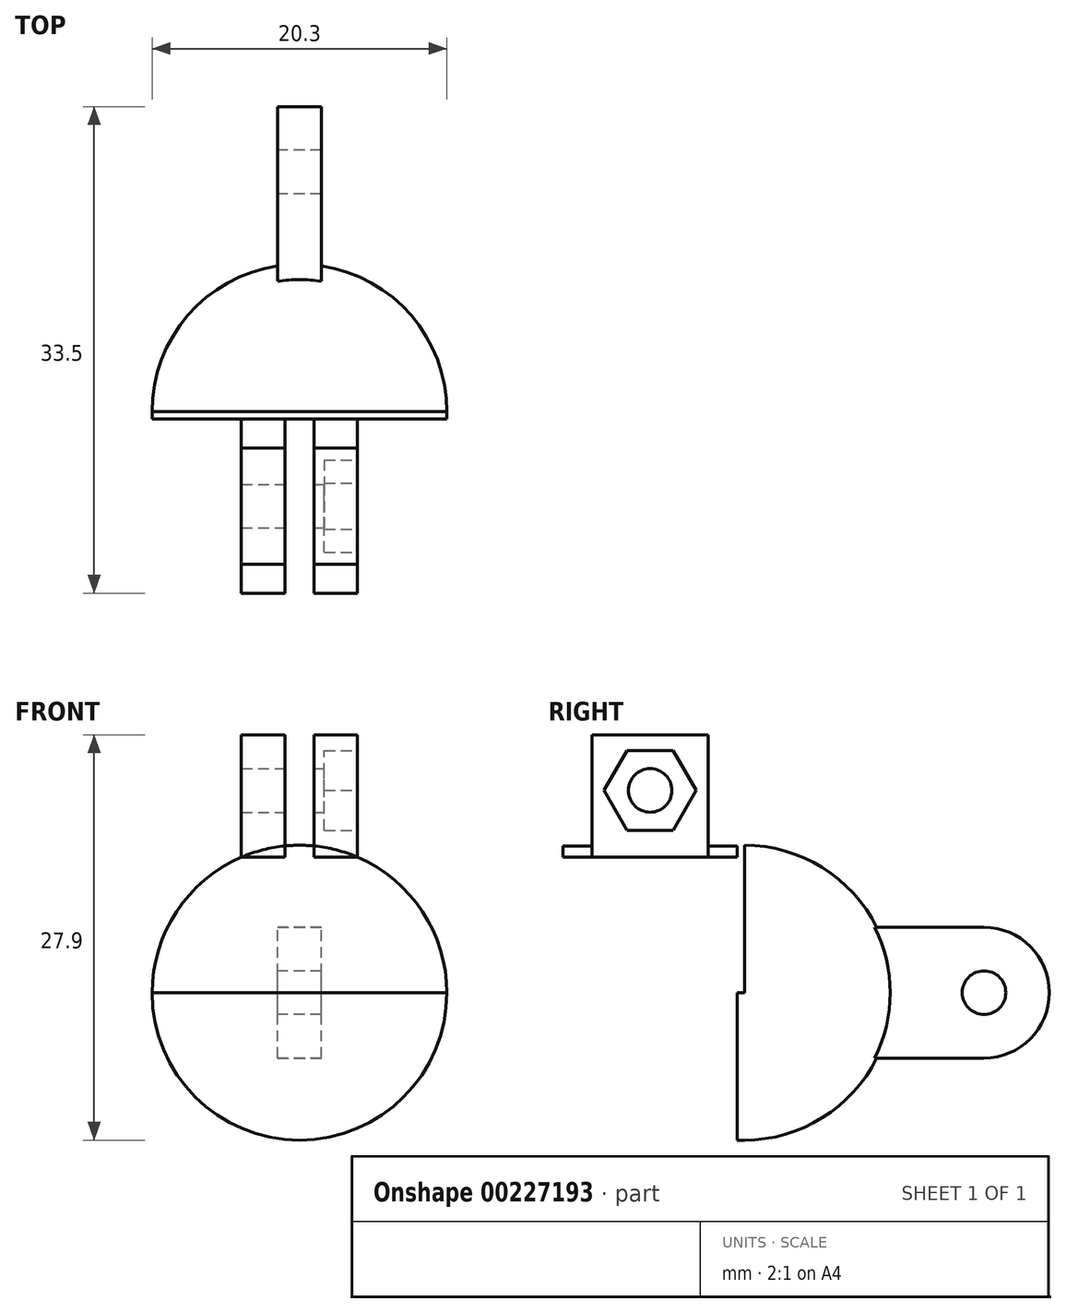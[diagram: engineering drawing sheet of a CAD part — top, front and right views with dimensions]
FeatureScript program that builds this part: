
annotation { "Feature Type Name" : "Feature", "Feature Type Description" : "" }
export const myFeature = defineFeature(function(context is Context, id is Id, definition is map)
    precondition{}
    {
        {
            var Q0;
            Q0=qCreatedBy(makeId("Front.planeOp"),FACE);
            var sketch = newSketch(context, id + "F0", { "sketchPlane" : qUnion([Q0])});
            skCircle(sketch, "E0", {"center": v(0, 0) * mm, "radius": 5.15 * mm});
            skCircle(sketch, "E1", {"center": v(0, 0) * mm, "radius": 10.15 * mm});
            skLineSegment(sketch, "E2.bottom", {"start": v(-1, 5.05) * mm, "end": v(1, 5.05) * mm});
            skLineSegment(sketch, "E2.top", {"start": v(-1, 15.25) * mm, "end": v(1, 15.25) * mm});
            skLineSegment(sketch, "E2.left", {"start": v(-1, 5.05) * mm, "end": v(-1, 15.25) * mm});
            skLineSegment(sketch, "E2.right", {"start": v(1, 5.05) * mm, "end": v(1, 15.25) * mm});
            skPoint(sketch, "E2.middle", {"position": v(0, 10.15) * mm});
            skLineSegment(sketch, "E3.bottom", {"start": v(-1, 15.25) * mm, "end": v(-4, 15.25) * mm});
            skLineSegment(sketch, "E3.top", {"start": v(-1, 9.33) * mm, "end": v(-4, 9.33) * mm});
            skLineSegment(sketch, "E3.left", {"start": v(-1, 15.25) * mm, "end": v(-1, 9.33) * mm});
            skLineSegment(sketch, "E3.right", {"start": v(-4, 15.25) * mm, "end": v(-4, 9.33) * mm});
            skLineSegment(sketch, "E4.bottom", {"start": v(1, 15.25) * mm, "end": v(4, 15.25) * mm});
            skLineSegment(sketch, "E4.top", {"start": v(1, 9.33) * mm, "end": v(4, 9.33) * mm});
            skLineSegment(sketch, "E4.left", {"start": v(1, 15.25) * mm, "end": v(1, 9.33) * mm});
            skLineSegment(sketch, "E4.right", {"start": v(4, 15.25) * mm, "end": v(4, 9.33) * mm});
            skLineSegment(sketch, "E5.bottom", {"start": v(-4, 17.75) * mm, "end": v(-1, 17.75) * mm});
            skLineSegment(sketch, "E5.top", {"start": v(-4, 15.25) * mm, "end": v(-1, 15.25) * mm});
            skLineSegment(sketch, "E5.left", {"start": v(-4, 17.75) * mm, "end": v(-4, 15.25) * mm});
            skLineSegment(sketch, "E5.right", {"start": v(-1, 17.75) * mm, "end": v(-1, 15.25) * mm});
            skLineSegment(sketch, "E6.bottom", {"start": v(4, 17.75) * mm, "end": v(1, 17.75) * mm});
            skLineSegment(sketch, "E6.top", {"start": v(4, 15.25) * mm, "end": v(1, 15.25) * mm});
            skLineSegment(sketch, "E6.left", {"start": v(4, 17.75) * mm, "end": v(4, 15.25) * mm});
            skLineSegment(sketch, "E6.right", {"start": v(1, 17.75) * mm, "end": v(1, 15.25) * mm});
            skSolve(sketch);
        }
        {
            var Q0;
            {var subQ0=sQuery(id+"F0.wireOp",EDGE,"E3.top");Q0=makeQuery(id+"F0.imprint","IMPRINT",FACE,{"disambiguationData":[TD([[makeQuery(id+"F0.imprint","IMPRINT",EDGE,{"derivedFrom":subQ0}),-1.0]])]});}
            var Q1;
            {var subQ0=sQuery(id+"F0.wireOp",EDGE,"E4.top");Q1=makeQuery(id+"F0.imprint","IMPRINT",FACE,{"disambiguationData":[TD([[makeQuery(id+"F0.imprint","IMPRINT",EDGE,{"derivedFrom":subQ0}),1.0]])]});}
            var Q2;
            {var subQ1=sQuery(id+"F0.wireOp",EDGE,"E2.left");Q2=makeQuery(id+"F0.imprint","IMPRINT",FACE,{"disambiguationData":[TD([[makeQuery(id+"F0.imprint","IMPRINT",EDGE,{"derivedFrom":subQ1}),1.0]])]});}
            extrude(context, id + "F1", {"entities" : qUnion([Q0, Q1, Q2]), "depth" : 12 * mm});
        }
        {
            var Q0;
            {var subQ4=sQuery(id+"F0.wireOp",EDGE,"E3.bottom");Q0=makeQuery(id+"F0.imprint","IMPRINT",FACE,{"disambiguationData":[TD([[makeQuery(id+"F0.imprint","IMPRINT",EDGE,{"derivedFrom":subQ4}),1.0]])]});}
            var Q1;
            {var subQ4=sQuery(id+"F0.wireOp",EDGE,"E4.bottom");Q1=makeQuery(id+"F0.imprint","IMPRINT",FACE,{"disambiguationData":[TD([[makeQuery(id+"F0.imprint","IMPRINT",EDGE,{"derivedFrom":subQ4}),-1.0]])]});}
            var Q2;
            Q2=makeQuery(id+"F0.imprint","IMPRINT",FACE,{"disambiguationData":[TD([[makeQuery(id+"F0.imprint","IMPRINT",EDGE,{"derivedFrom":sQuery(id+"F0.wireOp",EDGE,"E5.bottom")}),-1.0]])]});
            var Q3;
            {var subQ0=sQuery(id+"F0.wireOp",EDGE,"E3.right");Q3=makeQuery(id+"F0.imprint","IMPRINT",FACE,{"disambiguationData":[TD([[makeQuery(id+"F0.imprint","IMPRINT",EDGE,{"derivedFrom":subQ0}),1.0]])]});}
            var Q4;
            {var subQ0=sQuery(id+"F0.wireOp",EDGE,"E4.right");Q4=makeQuery(id+"F0.imprint","IMPRINT",FACE,{"disambiguationData":[TD([[makeQuery(id+"F0.imprint","IMPRINT",EDGE,{"derivedFrom":subQ0}),-1.0]])]});}
            var Q5;
            Q5=makeQuery(id+"F0.imprint","IMPRINT",FACE,{"disambiguationData":[TD([[makeQuery(id+"F0.imprint","IMPRINT",EDGE,{"derivedFrom":sQuery(id+"F0.wireOp",EDGE,"E6.bottom")}),1.0]])]});
            extrude(context, id + "F2", {"entities" : qUnion([Q0, Q1, Q2, Q3, Q4, Q5]), "operationType" : NewBodyOperationType.ADD, "depth" : 10 * mm});
        }
        {
            var Q0;
            {var subQ4=sQuery(id+"F0.wireOp",EDGE,"E3.bottom");Q0=makeQuery(id+"F0.imprint","IMPRINT",FACE,{"disambiguationData":[TD([[makeQuery(id+"F0.imprint","IMPRINT",EDGE,{"derivedFrom":subQ4}),1.0]])]});}
            var Q1;
            {var subQ4=sQuery(id+"F0.wireOp",EDGE,"E4.bottom");Q1=makeQuery(id+"F0.imprint","IMPRINT",FACE,{"disambiguationData":[TD([[makeQuery(id+"F0.imprint","IMPRINT",EDGE,{"derivedFrom":subQ4}),-1.0]])]});}
            var Q2;
            Q2=makeQuery(id+"F0.imprint","IMPRINT",FACE,{"disambiguationData":[TD([[makeQuery(id+"F0.imprint","IMPRINT",EDGE,{"derivedFrom":sQuery(id+"F0.wireOp",EDGE,"E5.bottom")}),-1.0]])]});
            var Q3;
            {var subQ0=sQuery(id+"F0.wireOp",EDGE,"E3.right");Q3=makeQuery(id+"F0.imprint","IMPRINT",FACE,{"disambiguationData":[TD([[makeQuery(id+"F0.imprint","IMPRINT",EDGE,{"derivedFrom":subQ0}),1.0]])]});}
            var Q4;
            Q4=makeQuery(id+"F0.imprint","IMPRINT",FACE,{"disambiguationData":[TD([[makeQuery(id+"F0.imprint","IMPRINT",EDGE,{"derivedFrom":sQuery(id+"F0.wireOp",EDGE,"E6.bottom")}),1.0]])]});
            var Q5;
            {var subQ0=sQuery(id+"F0.wireOp",EDGE,"E4.right");Q5=makeQuery(id+"F0.imprint","IMPRINT",FACE,{"disambiguationData":[TD([[makeQuery(id+"F0.imprint","IMPRINT",EDGE,{"derivedFrom":subQ0}),-1.0]])]});}
            extrude(context, id + "F3", {"entities" : qUnion([Q0, Q1, Q2, Q3, Q4, Q5]), "operationType" : NewBodyOperationType.REMOVE, "depth" : 2 * mm});
        }
        {
            var Q0;
            Q0=makeQuery(id+"F2.opExtrude","SWEPT_FACE",FACE,{"disambiguationData":[OSD([sQuery(id+"F0.wireOp",EDGE,"E4.right")])]});
            var sketch = newSketch(context, id + "F4", { "sketchPlane" : qUnion([Q0])});
            skSolve(sketch);
        }
        {
            var Q0;
            {var subQ0=sQuery(id+"F0.wireOp",EDGE,"E4.right");Q0=makeQuery(id+"F4.imprint","IMPRINT",FACE,{"disambiguationData":[TD([[makeQuery(id+"F4.imprint","IMPRINT",EDGE,{"derivedFrom":makeQuery(id+"F2.opExtrude","CAP_EDGE",EDGE,{"disambiguationData":[OSD([subQ0])],"isStart":false})}),1.0]])]});}
            var sketch = newSketch(context, id + "F5", { "sketchPlane" : qUnion([Q0])});
            skLineSegment(sketch, "E7.0", {"start": v(-12, 10.1) * mm, "end": v(-10, 10.1) * mm});
            skLineSegment(sketch, "E8", {"start": v(-10, 10.1) * mm, "end": v(0, 10.1) * mm});
            skLineSegment(sketch, "E9.0", {"start": v(-10, 17.75) * mm, "end": v(-2, 17.75) * mm});
            skLineSegment(sketch, "E10", {"start": v(-6, 17.75) * mm, "end": v(-6, 10.1) * mm, "construction": true});
            skCircle(sketch, "E11", {"center": v(-6, 13.92) * mm, "radius": 1.5 * mm});
            skCircle(sketch, "E12.cCircle", {"center": v(-6, 13.92) * mm, "radius": 2.75 * mm, "construction": true});
            skLineSegment(sketch, "E12.0", {"start": v(-7.59, 16.67) * mm, "end": v(-4.41, 16.67) * mm});
            skLineSegment(sketch, "E12.1", {"start": v(-4.41, 16.67) * mm, "end": v(-2.82, 13.92) * mm});
            skLineSegment(sketch, "E12.2", {"start": v(-2.82, 13.92) * mm, "end": v(-4.41, 11.17) * mm});
            skLineSegment(sketch, "E12.3", {"start": v(-4.41, 11.17) * mm, "end": v(-7.59, 11.17) * mm});
            skLineSegment(sketch, "E12.4", {"start": v(-7.59, 11.17) * mm, "end": v(-9.18, 13.92) * mm});
            skLineSegment(sketch, "E12.5", {"start": v(-9.18, 13.92) * mm, "end": v(-7.59, 16.67) * mm});
            skPoint(sketch, "E12.0.midPoint", {"position": v(-6, 16.67) * mm});
            skSolve(sketch);
        }
        {
            var Q0;
            Q0=makeQuery(id+"F5.imprint","IMPRINT",FACE,{"disambiguationData":[TD([[makeQuery(id+"F5.imprint","IMPRINT",EDGE,{"derivedFrom":sQuery(id+"F5.wireOp",EDGE,"E11")}),1.0]])]});
            extrude(context, id + "F6", {"entities" : qUnion([Q0]), "operationType" : NewBodyOperationType.REMOVE, "oppositeDirection" : true, "depth" : 25 * mm});
        }
        {
            var Q0;
            Q0=makeQuery(id+"F5.imprint","IMPRINT",FACE,{"disambiguationData":[TD([[makeQuery(id+"F5.imprint","IMPRINT",EDGE,{"derivedFrom":sQuery(id+"F5.wireOp",EDGE,"E11")}),-1.0]])]});
            extrude(context, id + "F7", {"entities" : qUnion([Q0]), "operationType" : NewBodyOperationType.REMOVE, "oppositeDirection" : true, "depth" : 2.3 * mm});
        }
        {
            var Q0;
            {var subQ1=sQuery(id+"F0.wireOp",EDGE,"E2.left");Q0=makeQuery(id+"F0.imprint","IMPRINT",FACE,{"disambiguationData":[TD([[makeQuery(id+"F0.imprint","IMPRINT",EDGE,{"derivedFrom":subQ1}),1.0]])]});}
            var sketch = newSketch(context, id + "F8", { "sketchPlane" : qUnion([Q0])});
            skCircle(sketch, "E13.0", {"center": v(0, 0) * mm, "radius": 5.15 * mm});
            skCircle(sketch, "E14.0", {"center": v(0, 0) * mm, "radius": 10.15 * mm});
            skLineSegment(sketch, "E15", {"start": v(10.15, 0) * mm, "end": v(5.15, 0) * mm});
            skLineSegment(sketch, "E16", {"start": v(-5.15, 0) * mm, "end": v(-10.15, 0) * mm});
            skLineSegment(sketch, "E17", {"start": v(5.15, 0) * mm, "end": v(-5.15, 0) * mm});
            skSolve(sketch);
        }
        {
            var Q0;
            {var subQ1=sQuery(id+"F8.wireOp",EDGE,"E15");Q0=makeQuery(id+"F8.imprint","IMPRINT",FACE,{"disambiguationData":[TD([[makeQuery(id+"F8.imprint","IMPRINT",EDGE,{"derivedFrom":subQ1}),1.0]])]});}
            var Q1;
            {var subQ0=sQuery(id+"F8.wireOp",EDGE,"E17");Q1=makeQuery(id+"F8.imprint","IMPRINT",FACE,{"disambiguationData":[TD([[makeQuery(id+"F8.imprint","IMPRINT",EDGE,{"derivedFrom":subQ0}),1.0]])]});}
            extrude(context, id + "F9", {"entities" : qUnion([Q0, Q1]), "operationType" : NewBodyOperationType.ADD, "oppositeDirection" : true, "depth" : .5 * mm});
        }
        {
            var Q0;
            Q0=qCreatedBy(makeId("Right.planeOp"),FACE);
            var sketch = newSketch(context, id + "F10", { "sketchPlane" : qUnion([Q0])});
            skLineSegment(sketch, "E18", {"start": v(0, 0) * mm, "end": v(17, 0) * mm});
            skCircle(sketch, "E19", {"center": v(17, 0) * mm, "radius": 1.5 * mm});
            skCircle(sketch, "E20", {"center": v(17, 0) * mm, "radius": 4.5 * mm});
            skLineSegment(sketch, "E21.0", {"start": v(-10, 10.1) * mm, "end": v(0, 10.1) * mm});
            skLineSegment(sketch, "E22.0", {"start": v(0, -10.15) * mm, "end": v(0, 10.15) * mm});
            skCircle(sketch, "E23", {"center": v(0, 0) * mm, "radius": 10.15 * mm});
            skLineSegment(sketch, "E24", {"start": v(17, 0) * mm, "end": v(17, 4.5) * mm});
            skLineSegment(sketch, "E25", {"start": v(17, 4.5) * mm, "end": v(9.1, 4.5) * mm});
            skLineSegment(sketch, "E26.MirrorCS", {"start": v(17, -4.5) * mm, "end": v(9.1, -4.5) * mm});
            skLineSegment(sketch, "E27.0", {"start": v(0.5, 0) * mm, "end": v(0.5, -10.15) * mm});
            skLineSegment(sketch, "E28", {"start": v(0.5, 0) * mm, "end": v(0.5, 10.14) * mm});
            skLineSegment(sketch, "E29", {"start": v(9.1, -4.5) * mm, "end": v(9.1, 4.5) * mm});
            skSolve(sketch);
        }
        {
            var Q0;
            Q0=makeQuery(id+"F9.opExtrude","CAP_FACE",FACE,{"disambiguationData":[OSD([sQuery(id+"F8.wireOp",EDGE,"E14.0"),sQuery(id+"F8.wireOp",EDGE,"E15"),sQuery(id+"F8.wireOp",EDGE,"E16"),sQuery(id+"F8.wireOp",EDGE,"E17")])],"isStart":false});
            var Q1;
            Q1=makeQuery(id+"F9.opExtrude","CAP_EDGE",EDGE,{"disambiguationData":[OSD([sQuery(id+"F8.wireOp",EDGE,"E14.0")])],"isStart":false});
            var Q2;
            Q2=makeQuery(id+"F9.opExtrude","CAP_EDGE",EDGE,{"disambiguationData":[OSD([sQuery(id+"F8.wireOp",EDGE,"E15"),sQuery(id+"F8.wireOp",EDGE,"E16"),sQuery(id+"F8.wireOp",EDGE,"E17")])],"isStart":false});
            revolve(context, id + "F11", {"operationType" : NewBodyOperationType.ADD, "entities" : qUnion([Q0]), "surfaceEntities" : qUnion([Q1]), "axis" : qUnion([Q2]), "revolveType" : RevolveType.ONE_DIRECTION, "oppositeDirection" : true, "angle" : 180 * degree});
        }
        {
            var Q0;
            {var subQ0=sQuery(id+"F10.wireOp",EDGE,"E20");var subQ1=sQuery(id+"F10.wireOp",EDGE,"E18");var subQ2=makeQuery(id+"F10.imprint","INTERSECT",VERTEX,{"derivedFrom":[subQ1,subQ0]});Q0=makeQuery(id+"F10.imprint","IMPRINT",FACE,{"disambiguationData":[TD([[makeQuery(id+"F10.imprint","IMPRINT",EDGE,{"disambiguationData":[TD([[subQ2,-1.0]])],"derivedFrom":subQ1}),1.0]])]});}
            var Q1;
            {var subQ5=sQuery(id+"F10.wireOp",EDGE,"E25");Q1=makeQuery(id+"F10.imprint","IMPRINT",FACE,{"disambiguationData":[TD([[makeQuery(id+"F10.imprint","IMPRINT",EDGE,{"derivedFrom":subQ5}),1.0]])]});}
            var Q2;
            {var subQ5=sQuery(id+"F10.wireOp",EDGE,"E26.MirrorCS");Q2=makeQuery(id+"F10.imprint","IMPRINT",FACE,{"disambiguationData":[TD([[makeQuery(id+"F10.imprint","IMPRINT",EDGE,{"derivedFrom":subQ5}),-1.0]])]});}
            var Q3;
            {var subQ1=sQuery(id+"F10.wireOp",EDGE,"E20");var subQ5=sQuery(id+"F10.wireOp",EDGE,"E18");var subQ8=makeQuery(id+"F10.imprint","INTERSECT",VERTEX,{"derivedFrom":[subQ5,subQ1]});Q3=makeQuery(id+"F10.imprint","IMPRINT",FACE,{"disambiguationData":[TD([[makeQuery(id+"F10.imprint","IMPRINT",EDGE,{"disambiguationData":[TD([[subQ8,-1.0]])],"derivedFrom":subQ5}),-1.0]])]});}
            extrude(context, id + "F12", {"entities" : qUnion([Q0, Q1, Q2, Q3]), "operationType" : NewBodyOperationType.ADD, "endBound" : BoundingType.SYMMETRIC, "depth" : 3 * mm});
        }
    });
